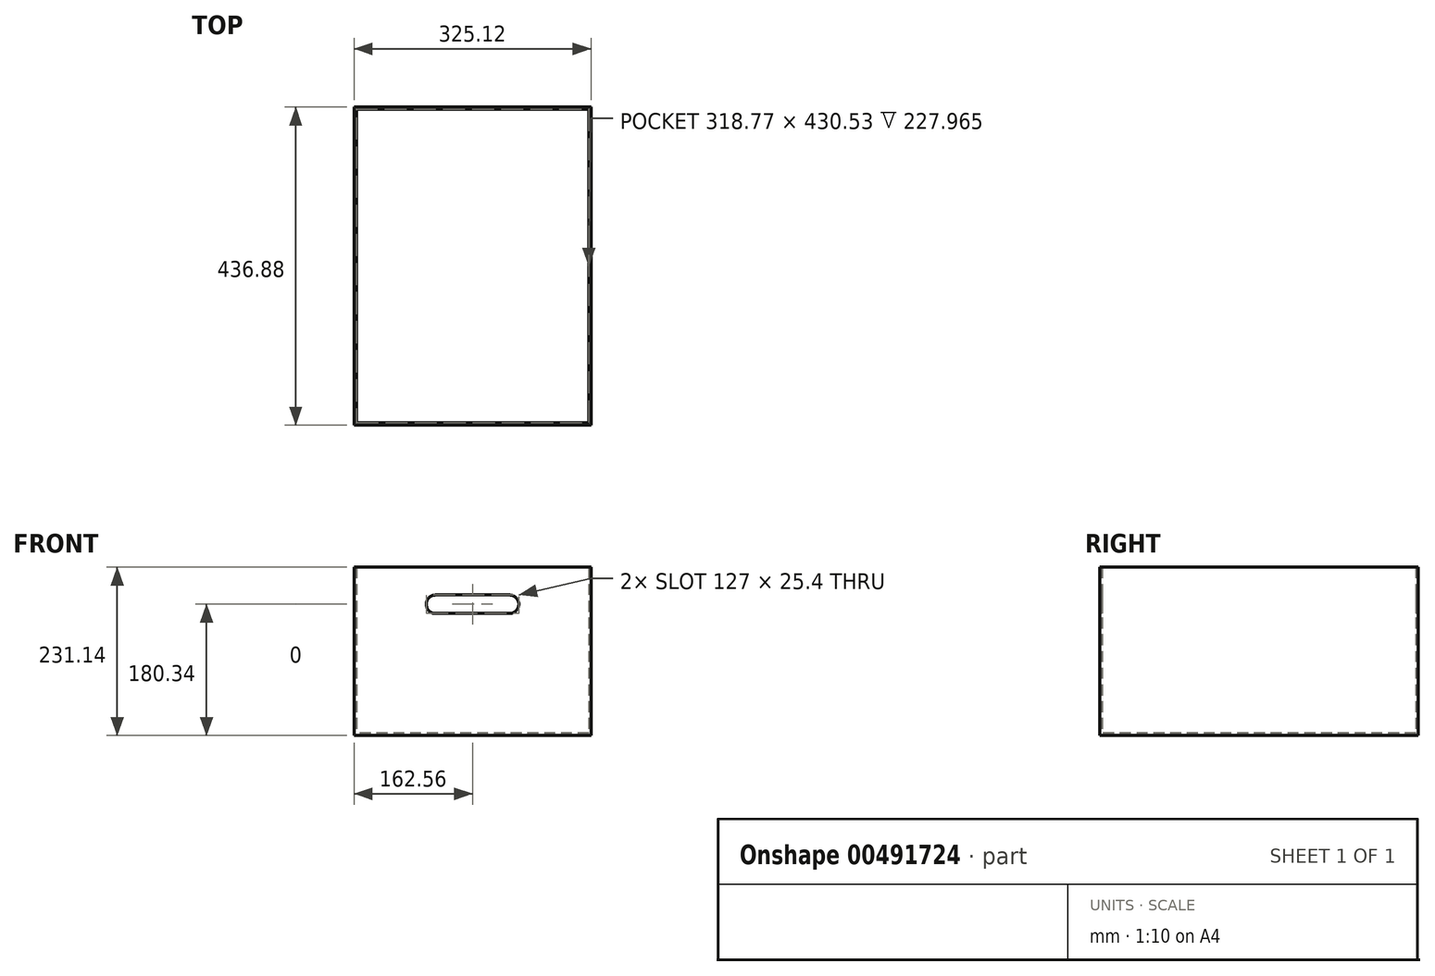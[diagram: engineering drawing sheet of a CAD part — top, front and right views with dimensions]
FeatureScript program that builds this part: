
annotation { "Feature Type Name" : "Feature", "Feature Type Description" : "" }
export const myFeature = defineFeature(function(context is Context, id is Id, definition is map)
    precondition{}
    {
        {
            var Q0;
            Q0=qCreatedBy(makeId("Top.planeOp"),FACE);
            var sketch = newSketch(context, id + "F0", { "sketchPlane" : qUnion([Q0])});
            skLineSegment(sketch, "E0.bottom", {"start": v(162.56, 218.44) * mm, "end": v(-162.56, 218.44) * mm});
            skLineSegment(sketch, "E0.top", {"start": v(162.56, -218.44) * mm, "end": v(-162.56, -218.44) * mm});
            skLineSegment(sketch, "E0.left", {"start": v(162.56, 218.44) * mm, "end": v(162.56, -218.44) * mm});
            skLineSegment(sketch, "E0.right", {"start": v(-162.56, 218.44) * mm, "end": v(-162.56, -218.44) * mm});
            skPoint(sketch, "E0.middle", {"position": v(0, 0) * mm});
            skSolve(sketch);
        }
        {
            var Q0;
            Q0 = qSketchRegion(id + "F0", true);
            extrude(context, id + "F1", {"entities" : qUnion([Q0]), "depth" : 231.14 * mm});
        }
        {
            var Q0;
            Q0=makeQuery(id+"F1.opExtrude","CAP_FACE",FACE,{"disambiguationData":[OSD([sQuery(id+"F0.wireOp",EDGE,"E0.bottom"),sQuery(id+"F0.wireOp",EDGE,"E0.top"),sQuery(id+"F0.wireOp",EDGE,"E0.left"),sQuery(id+"F0.wireOp",EDGE,"E0.right")])],"isStart":false});
            shell(context, id + "F2", {"entities" : qUnion([Q0]), "thickness" : 3.17 * mm});
        }
        {
            var Q0;
            Q0=makeQuery(id+"F1.opExtrude","SWEPT_FACE",FACE,{"disambiguationData":[OSD([sQuery(id+"F0.wireOp",EDGE,"E0.top")])]});
            var sketch = newSketch(context, id + "F3", { "sketchPlane" : qUnion([Q0])});
            skLineSegment(sketch, "E1", {"start": v(0, 231.14) * mm, "end": v(0, 180.34) * mm, "construction": true});
            skPoint(sketch, "E1.endSnap0", {"position": v(0, 231.14) * mm});
            skLineSegment(sketch, "E2", {"start": v(-50.8, 180.34) * mm, "end": v(50.8, 180.34) * mm, "construction": true});
            skArc(sketch, "E3.0.startCap", {"start": v(-50.8, 167.64) * mm, "mid": v(-63.5, 180.34) * mm, "end": v(-50.8, 193.04) * mm});
            skArc(sketch, "E3.0.endCap", {"start": v(50.8, 193.04) * mm, "mid": v(63.5, 180.34) * mm, "end": v(50.8, 167.64) * mm});
            skLineSegment(sketch, "E3.0.left", {"start": v(-50.8, 193.04) * mm, "end": v(50.8, 193.04) * mm});
            skLineSegment(sketch, "E3.0.right", {"start": v(-50.8, 167.64) * mm, "end": v(50.8, 167.64) * mm});
            skSolve(sketch);
        }
        {
            var Q0;
            Q0 = qSketchRegion(id + "F3", true);
            extrude(context, id + "F4", {"entities" : qUnion([Q0]), "operationType" : NewBodyOperationType.REMOVE, "endBound" : BoundingType.THROUGH_ALL, "oppositeDirection" : true, "depth" : 25.4 * mm});
        }
    });
